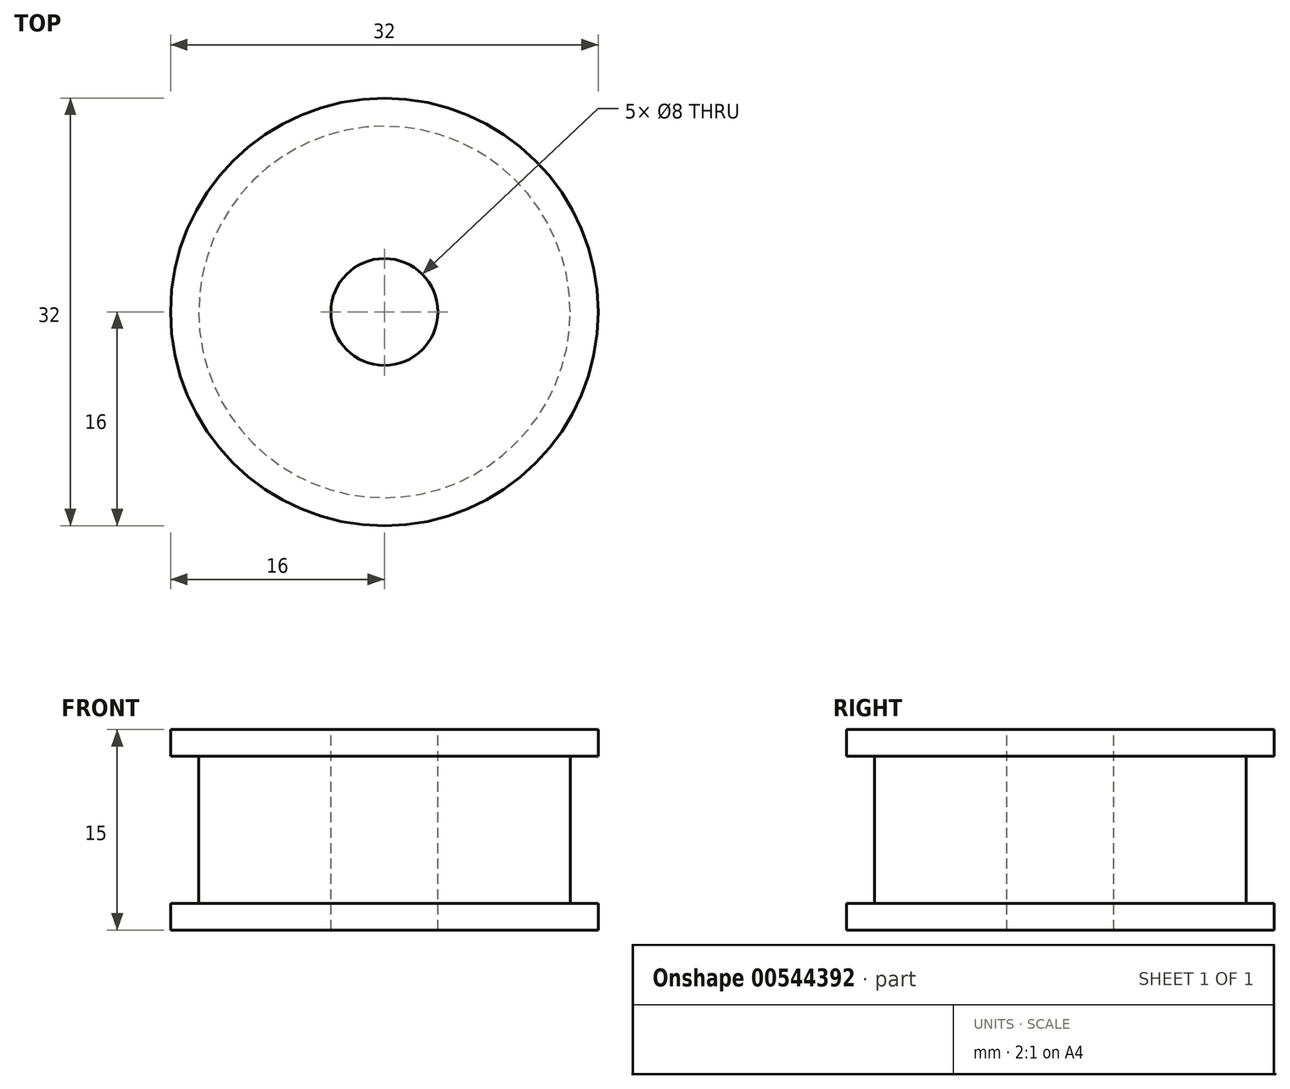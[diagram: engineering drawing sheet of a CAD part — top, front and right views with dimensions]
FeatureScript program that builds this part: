
annotation { "Feature Type Name" : "Feature", "Feature Type Description" : "" }
export const myFeature = defineFeature(function(context is Context, id is Id, definition is map)
    precondition{}
    {
        {
            var Q0;
            Q0=qCreatedBy(makeId("Front.planeOp"),FACE);
            var sketch = newSketch(context, id + "F0", { "sketchPlane" : qUnion([Q0])});
            skLineSegment(sketch, "E0", {"start": v(0, 9.5) * mm, "end": v(0, -8.32) * mm, "construction": true});
            skLineSegment(sketch, "E1", {"start": v(4, 7.5) * mm, "end": v(16, 7.5) * mm});
            skLineSegment(sketch, "E2", {"start": v(16, 7.5) * mm, "end": v(16, 5.5) * mm});
            skLineSegment(sketch, "E3", {"start": v(16, 5.5) * mm, "end": v(13.9, 5.5) * mm});
            skLineSegment(sketch, "E4", {"start": v(13.9, 5.5) * mm, "end": v(13.9, -5.5) * mm});
            skLineSegment(sketch, "E5", {"start": v(13.9, -5.5) * mm, "end": v(16, -5.5) * mm});
            skLineSegment(sketch, "E6", {"start": v(16, -5.5) * mm, "end": v(16, -7.5) * mm});
            skLineSegment(sketch, "E7", {"start": v(16, -7.5) * mm, "end": v(4, -7.5) * mm});
            skLineSegment(sketch, "E8", {"start": v(-6.47, 0) * mm, "end": v(20.28, 0) * mm, "construction": true});
            skLineSegment(sketch, "E9", {"start": v(4, 7.5) * mm, "end": v(4, -7.5) * mm});
            skSolve(sketch);
        }
        {
            var Q0;
            Q0 = qSketchRegion(id + "F0", true);
            var Q1;
            Q1=sQuery(id+"F0.wireOp",EDGE,"E0");
            revolve(context, id + "F1", {"entities" : qUnion([Q0]), "axis" : qUnion([Q1]), "revolveType" : RevolveType.FULL});
        }
    });
